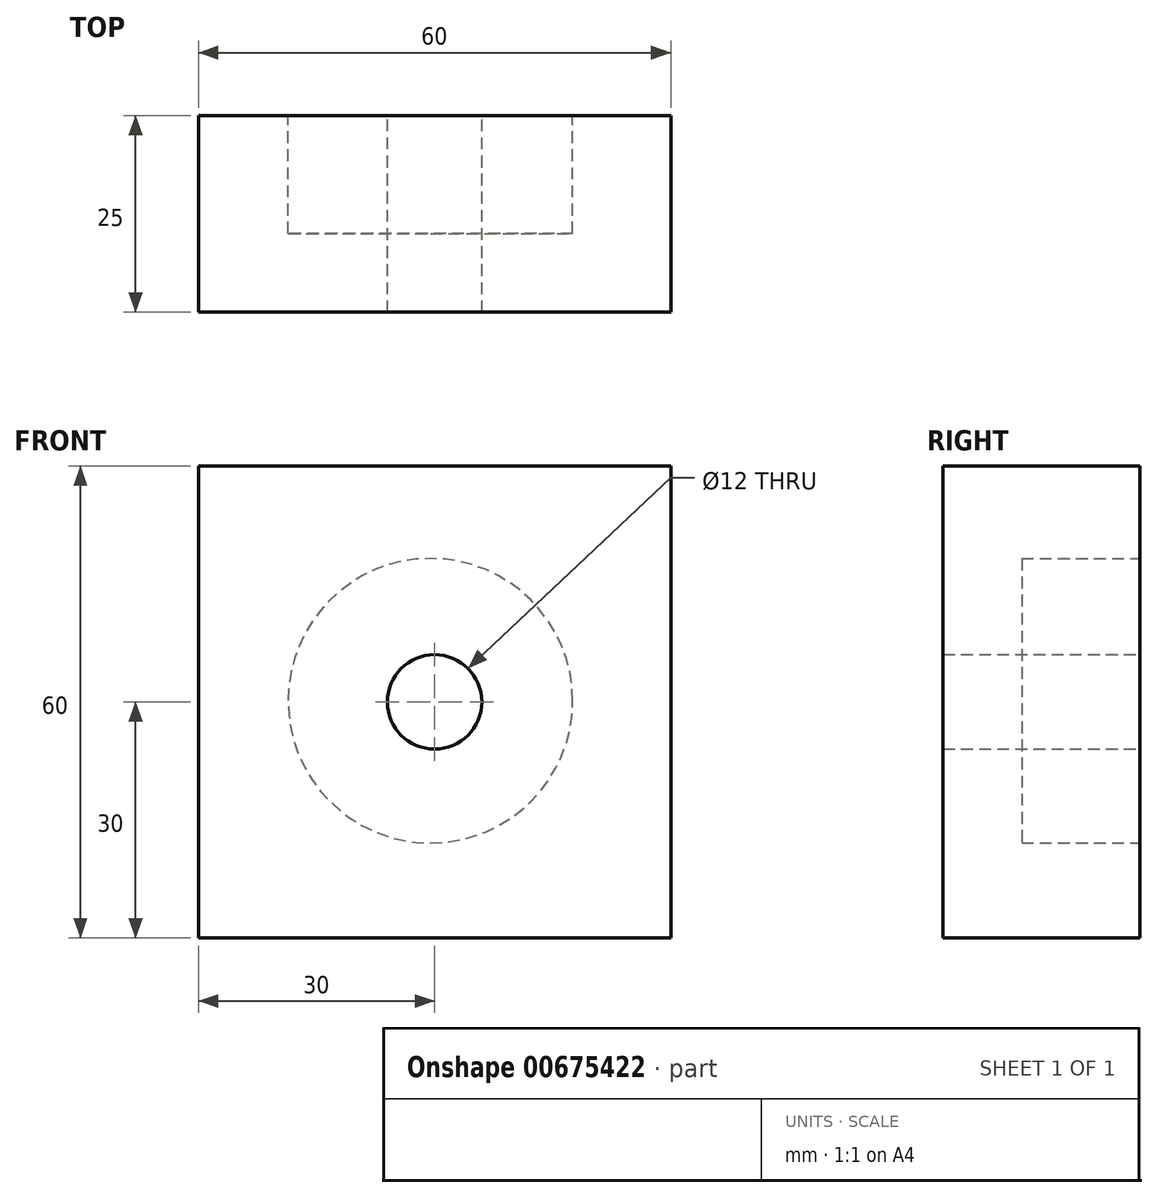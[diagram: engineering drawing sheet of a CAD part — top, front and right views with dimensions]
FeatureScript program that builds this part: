
annotation { "Feature Type Name" : "Feature", "Feature Type Description" : "" }
export const myFeature = defineFeature(function(context is Context, id is Id, definition is map)
    precondition{}
    {
        {
            var Q0;
            Q0=qCreatedBy(makeId("Front.planeOp"),FACE);
            var sketch = newSketch(context, id + "F0", { "sketchPlane" : qUnion([Q0])});
            skCircle(sketch, "E0", {"center": v(0, 0) * mm, "radius": 6 * mm});
            skLineSegment(sketch, "E1.bottom", {"start": v(0, 0) * mm, "end": v(-30, 0) * mm});
            skLineSegment(sketch, "E1.top", {"start": v(0, 30) * mm, "end": v(-30, 30) * mm});
            skLineSegment(sketch, "E1.left", {"start": v(0, 0) * mm, "end": v(0, 30) * mm});
            skLineSegment(sketch, "E1.right", {"start": v(-30, 0) * mm, "end": v(-30, 30) * mm});
            skLineSegment(sketch, "E2.bottom", {"start": v(0, 30) * mm, "end": v(30, 30) * mm});
            skLineSegment(sketch, "E2.top", {"start": v(0, 0) * mm, "end": v(30, 0) * mm});
            skLineSegment(sketch, "E2.left", {"start": v(0, 30) * mm, "end": v(0, 0) * mm});
            skLineSegment(sketch, "E2.right", {"start": v(30, 30) * mm, "end": v(30, 0) * mm});
            skLineSegment(sketch, "E3.bottom", {"start": v(-30, 0) * mm, "end": v(0, 0) * mm});
            skLineSegment(sketch, "E3.top", {"start": v(-30, -30) * mm, "end": v(0, -30) * mm});
            skLineSegment(sketch, "E3.left", {"start": v(-30, 0) * mm, "end": v(-30, -30) * mm});
            skLineSegment(sketch, "E3.right", {"start": v(0, 0) * mm, "end": v(0, -30) * mm});
            skLineSegment(sketch, "E4.top", {"start": v(0, -30) * mm, "end": v(30, -30) * mm});
            skLineSegment(sketch, "E4.right", {"start": v(30, 0) * mm, "end": v(30, -30) * mm});
            skSolve(sketch);
        }
        {
            var Q0;
            {var subQ1=sQuery(id+"F0.wireOp",EDGE,"E1.top");Q0=makeQuery(id+"F0.imprint","IMPRINT",FACE,{"disambiguationData":[TD([[makeQuery(id+"F0.imprint","IMPRINT",EDGE,{"derivedFrom":subQ1}),1.0]])]});}
            var Q1;
            {var subQ2=sQuery(id+"F0.wireOp",EDGE,"E2.bottom");Q1=makeQuery(id+"F0.imprint","IMPRINT",FACE,{"disambiguationData":[TD([[makeQuery(id+"F0.imprint","IMPRINT",EDGE,{"derivedFrom":subQ2}),-1.0]])]});}
            var Q2;
            {var subQ0=sQuery(id+"F0.wireOp",EDGE,"E4.top");Q2=makeQuery(id+"F0.imprint","IMPRINT",FACE,{"disambiguationData":[TD([[makeQuery(id+"F0.imprint","IMPRINT",EDGE,{"derivedFrom":subQ0}),1.0]])]});}
            var Q3;
            {var subQ6=sQuery(id+"F0.wireOp",EDGE,"E3.top");Q3=makeQuery(id+"F0.imprint","IMPRINT",FACE,{"disambiguationData":[TD([[makeQuery(id+"F0.imprint","IMPRINT",EDGE,{"derivedFrom":subQ6}),1.0]])]});}
            extrude(context, id + "F1", {"entities" : qUnion([Q0, Q1, Q2, Q3]), "depth" : 25 * mm, "offsetDistance" : 25 * mm});
        }
        {
            var Q0;
            Q0=makeQuery(id+"F1.opExtrude","CAP_FACE",FACE,{"disambiguationData":[OSD([sQuery(id+"F0.wireOp",EDGE,"E0"),sQuery(id+"F0.wireOp",EDGE,"E1.top"),sQuery(id+"F0.wireOp",EDGE,"E1.right"),sQuery(id+"F0.wireOp",EDGE,"E2.bottom"),sQuery(id+"F0.wireOp",EDGE,"E2.right"),sQuery(id+"F0.wireOp",EDGE,"E3.top"),sQuery(id+"F0.wireOp",EDGE,"E3.left"),sQuery(id+"F0.wireOp",EDGE,"E4.top"),sQuery(id+"F0.wireOp",EDGE,"E4.right")])],"isStart":true});
            var sketch = newSketch(context, id + "F2", { "sketchPlane" : qUnion([Q0])});
            skCircle(sketch, "E5", {"center": v(0.53, 0.15) * mm, "radius": 18.07 * mm});
            skCircle(sketch, "E6", {"center": v(0, 0) * mm, "radius": 11.16 * mm});
            skSolve(sketch);
        }
        {
            var Q0;
            Q0=makeQuery(id+"F2.imprint","IMPRINT",FACE,{"disambiguationData":[TD([[makeQuery(id+"F2.imprint","IMPRINT",EDGE,{"derivedFrom":sQuery(id+"F2.wireOp",EDGE,"E5")}),1.0]])]});
            var Q1;
            Q1=makeQuery(id+"F2.imprint","IMPRINT",FACE,{"disambiguationData":[TD([[makeQuery(id+"F2.imprint","IMPRINT",EDGE,{"derivedFrom":makeQuery(id+"F1.opExtrude","CAP_EDGE",EDGE,{"disambiguationData":[OSD([sQuery(id+"F0.wireOp",EDGE,"E0")])],"isStart":true})}),-1.0]])]});
            var Q2;
            Q2=makeQuery(id+"F2.imprint","IMPRINT",FACE,{"disambiguationData":[TD([[makeQuery(id+"F2.imprint","IMPRINT",EDGE,{"derivedFrom":sQuery(id+"F2.wireOp",EDGE,"E6")}),1.0]])]});
            extrude(context, id + "F3", {"entities" : qUnion([Q0, Q1, Q2]), "oppositeDirection" : true, "depth" : 15 * mm, "offsetDistance" : 25 * mm});
        }
    });
